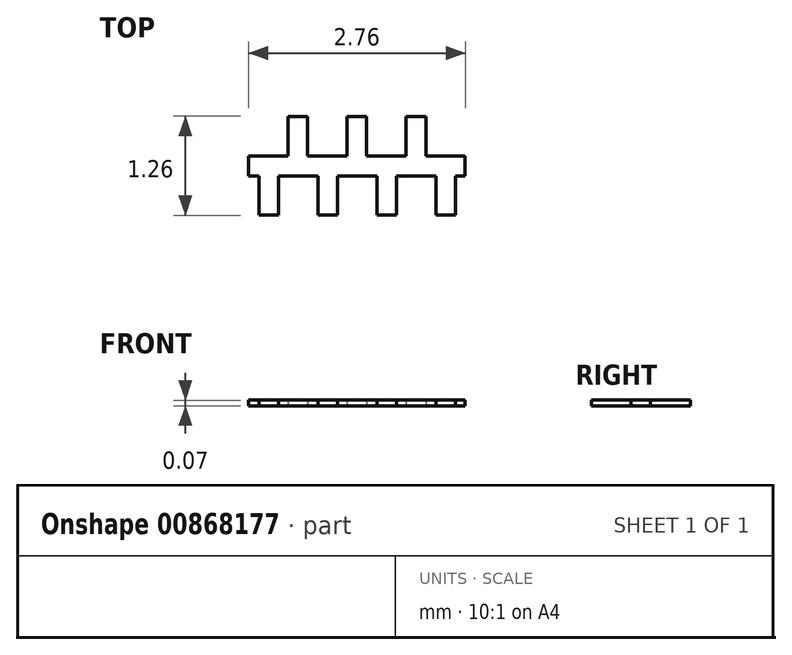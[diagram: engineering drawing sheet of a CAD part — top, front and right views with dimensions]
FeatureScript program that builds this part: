
annotation { "Feature Type Name" : "Feature", "Feature Type Description" : "" }
export const myFeature = defineFeature(function(context is Context, id is Id, definition is map)
    precondition{}
    {
        {
            var Q0;
            Q0=qCreatedBy(makeId("Top.planeOp"),FACE);
            var sketch = newSketch(context, id + "F0", { "sketchPlane" : qUnion([Q0])});
            skLineSegment(sketch, "E0", {"start": v(0, 0) * mm, "end": v(0, 0.25) * mm});
            skLineSegment(sketch, "E1", {"start": v(0, 0.25) * mm, "end": v(0.5, 0.25) * mm});
            skLineSegment(sketch, "E2", {"start": v(0.5, 0.25) * mm, "end": v(0.5, 0.76) * mm});
            skLineSegment(sketch, "E3", {"start": v(0.5, 0.76) * mm, "end": v(0.75, 0.76) * mm});
            skLineSegment(sketch, "E4", {"start": v(0.75, 0.76) * mm, "end": v(0.75, 0.25) * mm});
            skLineSegment(sketch, "E5", {"start": v(0.75, 0.25) * mm, "end": v(1.25, 0.25) * mm});
            skLineSegment(sketch, "E6", {"start": v(1.25, 0.25) * mm, "end": v(1.25, 0.76) * mm});
            skLineSegment(sketch, "E7", {"start": v(1.25, 0.76) * mm, "end": v(1.5, 0.76) * mm});
            skLineSegment(sketch, "E8", {"start": v(1.5, 0.76) * mm, "end": v(1.5, 0.25) * mm});
            skLineSegment(sketch, "E9", {"start": v(1.5, 0.25) * mm, "end": v(2, 0.25) * mm});
            skLineSegment(sketch, "E10", {"start": v(2, 0.25) * mm, "end": v(2, 0.76) * mm});
            skLineSegment(sketch, "E11", {"start": v(2, 0.76) * mm, "end": v(2.26, 0.76) * mm});
            skLineSegment(sketch, "E12", {"start": v(2.26, 0.76) * mm, "end": v(2.26, 0.25) * mm});
            skLineSegment(sketch, "E13", {"start": v(2.26, 0.25) * mm, "end": v(2.76, 0.25) * mm});
            skLineSegment(sketch, "E14", {"start": v(2.76, 0.25) * mm, "end": v(2.76, 0) * mm});
            skLineSegment(sketch, "E15", {"start": v(2.76, 0) * mm, "end": v(2.63, 0) * mm});
            skLineSegment(sketch, "E16", {"start": v(2.63, 0) * mm, "end": v(2.63, -0.5) * mm});
            skLineSegment(sketch, "E17", {"start": v(2.63, -0.5) * mm, "end": v(2.39, -0.5) * mm});
            skLineSegment(sketch, "E18", {"start": v(2.39, -0.5) * mm, "end": v(2.39, 0) * mm});
            skLineSegment(sketch, "E19", {"start": v(2.39, 0) * mm, "end": v(1.88, 0) * mm});
            skLineSegment(sketch, "E20", {"start": v(1.88, 0) * mm, "end": v(1.88, -0.5) * mm});
            skLineSegment(sketch, "E21", {"start": v(1.88, -0.5) * mm, "end": v(1.63, -0.5) * mm});
            skLineSegment(sketch, "E22", {"start": v(1.63, -0.5) * mm, "end": v(1.63, 0) * mm});
            skLineSegment(sketch, "E23", {"start": v(1.63, 0) * mm, "end": v(1.14, 0) * mm});
            skLineSegment(sketch, "E24", {"start": v(1.14, 0) * mm, "end": v(1.14, -0.5) * mm});
            skLineSegment(sketch, "E25", {"start": v(1.14, -0.5) * mm, "end": v(0.89, -0.5) * mm});
            skLineSegment(sketch, "E26", {"start": v(0.89, -0.5) * mm, "end": v(0.89, 0) * mm});
            skLineSegment(sketch, "E27", {"start": v(0.89, 0) * mm, "end": v(0.38, 0) * mm});
            skLineSegment(sketch, "E28", {"start": v(0.38, 0) * mm, "end": v(0.38, -0.5) * mm});
            skLineSegment(sketch, "E29", {"start": v(0.38, -0.5) * mm, "end": v(0.14, -0.5) * mm});
            skLineSegment(sketch, "E30", {"start": v(0.14, -0.5) * mm, "end": v(0.14, 0) * mm});
            skLineSegment(sketch, "E31", {"start": v(0.14, 0) * mm, "end": v(0, 0) * mm});
            skSolve(sketch);
        }
        {
            var Q0;
            Q0=makeQuery(id+"F0.imprint","IMPRINT",FACE,{"disambiguationData":[TD([[makeQuery(id+"F0.imprint","IMPRINT",EDGE,{"derivedFrom":sQuery(id+"F0.wireOp",EDGE,"E0")}),-1.0]])]});
            extrude(context, id + "F1", {"entities" : qUnion([Q0]), "depth" : 0.07 * mm, "offsetDistance" : 25 * mm});
        }
    });
